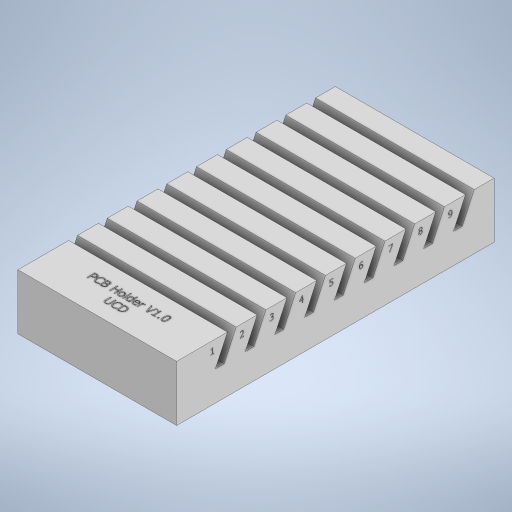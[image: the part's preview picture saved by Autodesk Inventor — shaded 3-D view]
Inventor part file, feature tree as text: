
AUTODESK INVENTOR PART (.ipt)
format: ipt  version: 2024 (Build 280153000, 153)  size: 1,226,752 bytes
history: native  units: mm
features: sketch x5, extrude x3, projected_geometry x3, emboss x2, plane x1, mirror x1
ambient origin geometry x8: Origin, YZ Plane, XZ Plane, XY Plane, X Axis, Y Axis, Z Axis, Center Point
bodies: Solid1 (feature_tree)
feature tree (15):
  extrude  "Extrusion1"  Depth=10.0mm
  extrude  "Extrusion2"  Depth=80.0mm TaperAngle=0.0deg
  emboss  "Emboss1"
  emboss  "Emboss2"
  extrude  "Extrusion3"  Depth=4.0mm
  plane  "Work Plane1"
  mirror  "Mirror1"
  sketch  "Sketch1"  dims[d0=10.0mm d1=18.0mm]
  sketch  "Sketch2"  dims[d2=160.0mm d3=80.0mm d4=0.0mm]
  projected_geometry  "Projected Loop1"
  sketch  "Sketch3"  dims[d5=5.0mm d6=4.0mm]
  projected_geometry  "Projected Loop2"
  sketch  "Sketch4"  dims[d7=10.0mm]
  projected_geometry  "Projected Loop3"
  sketch  "Sketch5"  dims[d8=100.0mm d10=15.0mm d11=10.0mm d13=10.0mm d15=11.34464mm d16=0.0mm d17=0.0mm d18=5.0mm d19=0.0mm d23=15.0mm d24=3.0mm d25=15.0mm d26=15.0mm d27=15.0mm d28=15.0mm d29=15.0mm d30=15.0mm d31=3.0mm d32=3.0mm d33=3.0mm d34=3.0mm d35=3.0mm d36=3.0mm d37=3.0mm d38=2.280541mm d41=6.5mm d42=15.0mm d43=3.0mm d44=5.0mm d45=0.0mm d46=10.0mm d47=5.0mm d48=0.0mm d49=-40.0mm]
